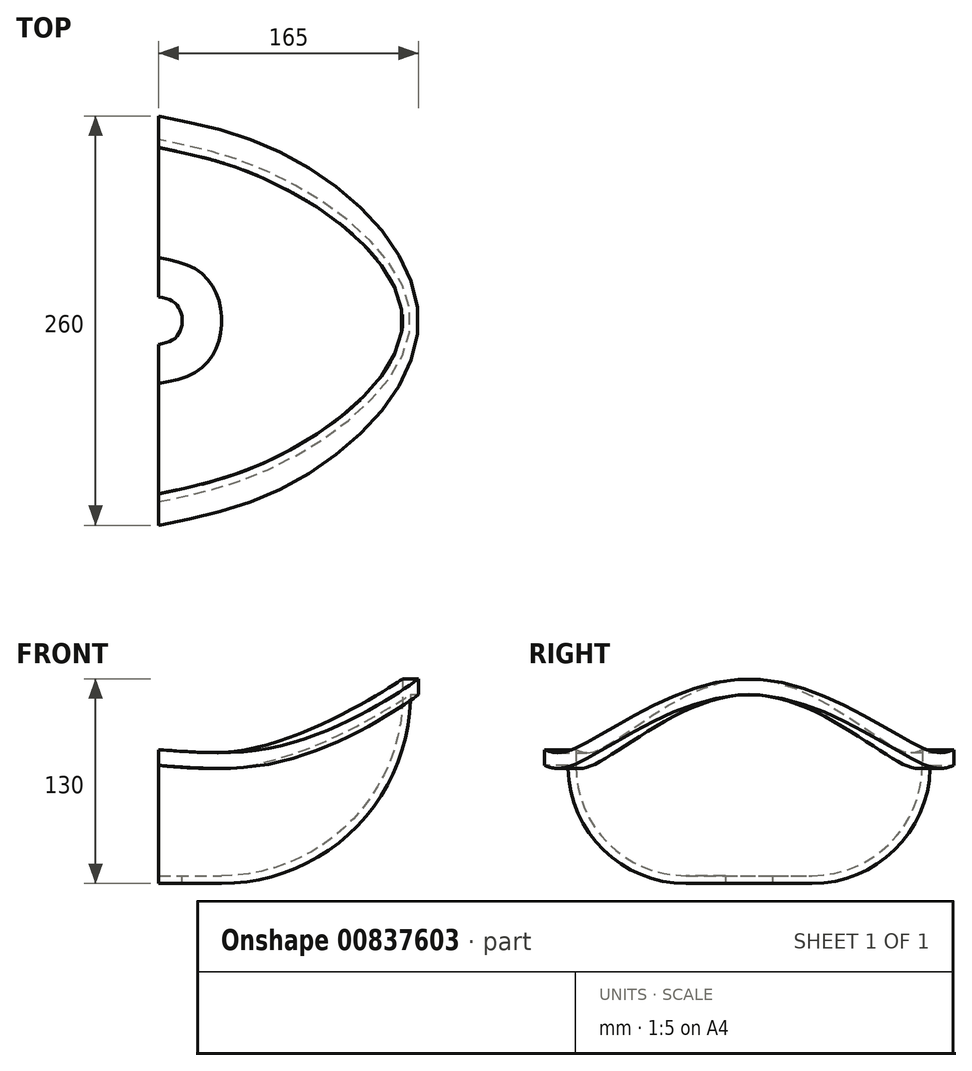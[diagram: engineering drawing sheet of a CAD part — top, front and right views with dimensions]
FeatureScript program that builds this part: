
annotation { "Feature Type Name" : "Feature", "Feature Type Description" : "" }
export const myFeature = defineFeature(function(context is Context, id is Id, definition is map)
    precondition{}
    {
        {
            var Q0;
            Q0=qCreatedBy(makeId("Front.planeOp"),FACE);
            var sketch = newSketch(context, id + "F0", { "sketchPlane" : qUnion([Q0])});
            skLineSegment(sketch, "E0.bottom", {"start": v(15, 5) * mm, "end": v(40, 5) * mm});
            skLineSegment(sketch, "E0.top", {"start": v(15, 0) * mm, "end": v(40, 0) * mm});
            skLineSegment(sketch, "E0.left", {"start": v(15, 5) * mm, "end": v(15, 0) * mm});
            skLineSegment(sketch, "E0.right", {"start": v(40, 5) * mm, "end": v(40, 0) * mm, "construction": true});
            skLineSegment(sketch, "E1.bottom", {"start": v(155, 130) * mm, "end": v(165, 130) * mm});
            skLineSegment(sketch, "E1.top", {"start": v(160, 120) * mm, "end": v(165, 120) * mm});
            skLineSegment(sketch, "E1.left", {"start": v(155, 130) * mm, "end": v(155, 120) * mm});
            skLineSegment(sketch, "E1.right", {"start": v(165, 130) * mm, "end": v(165, 120) * mm});
            skArc(sketch, "E2", {"start": v(40, 0) * mm, "mid": v(124.85, 35.15) * mm, "end": v(160, 120) * mm});
            skArc(sketch, "E3", {"start": v(40, 5) * mm, "mid": v(121.32, 38.68) * mm, "end": v(155, 120) * mm});
            skLineSegment(sketch, "E4", {"start": v(0, 0) * mm, "end": v(0, 50) * mm, "construction": true});
            skSolve(sketch);
        }
        {
            var Q0;
            Q0=sQuery(id+"F0.wireOp",EDGE,"E4");
            cPlane(context, id + "F1", {"entities" : qUnion([Q0]), "cplaneType" : CPlaneType.LINE_ANGLE, "offset" : 25 * mm, "angle" : 30 * degree, "oppositeDirection" : true, "width" : 150 * mm, "height" : 150 * mm});
        }
        {
            var Q0;
            Q0=qCreatedBy(id+"F1.planeOp",FACE);
            var sketch = newSketch(context, id + "F2", { "sketchPlane" : qUnion([Q0])});
            skLineSegment(sketch, "E5.bottom", {"start": v(15, 5) * mm, "end": v(40, 5) * mm});
            skLineSegment(sketch, "E5.top", {"start": v(15, 0) * mm, "end": v(40, 0) * mm});
            skLineSegment(sketch, "E5.left", {"start": v(15, 5) * mm, "end": v(15, 0) * mm});
            skLineSegment(sketch, "E5.right", {"start": v(40, 5) * mm, "end": v(40, 0) * mm, "construction": true});
            skLineSegment(sketch, "E6.bottom", {"start": v(110, 85) * mm, "end": v(130, 85) * mm});
            skLineSegment(sketch, "E6.top", {"start": v(115, 75) * mm, "end": v(130, 75) * mm});
            skLineSegment(sketch, "E6.left", {"start": v(110, 85) * mm, "end": v(110, 75) * mm});
            skLineSegment(sketch, "E6.right", {"start": v(130, 85) * mm, "end": v(130, 75) * mm});
            skArc(sketch, "E7", {"start": v(40, 0) * mm, "mid": v(93.03, 21.97) * mm, "end": v(115, 75) * mm});
            skArc(sketch, "E8", {"start": v(40, 5) * mm, "mid": v(89.5, 25.5) * mm, "end": v(110, 75) * mm});
            skLineSegment(sketch, "E9", {"start": v(0, 0) * mm, "end": v(0, 50) * mm, "construction": true});
            skSolve(sketch);
        }
        {
            var Q0;
            Q0=sQuery(id+"F0.wireOp",EDGE,"E4");
            cPlane(context, id + "F3", {"entities" : qUnion([Q0]), "cplaneType" : CPlaneType.LINE_ANGLE, "offset" : 25 * mm, "angle" : 150 * degree, "oppositeDirection" : true, "width" : 150 * mm, "height" : 150 * mm});
        }
        {
            var Q0;
            Q0=qCreatedBy(id+"F3.planeOp",FACE);
            var sketch = newSketch(context, id + "F4", { "sketchPlane" : qUnion([Q0])});
            skLineSegment(sketch, "E10.bottom", {"start": v(15, 5) * mm, "end": v(40, 5) * mm});
            skLineSegment(sketch, "E10.top", {"start": v(15, 0) * mm, "end": v(40, 0) * mm});
            skLineSegment(sketch, "E10.left", {"start": v(15, 5) * mm, "end": v(15, 0) * mm});
            skLineSegment(sketch, "E10.right", {"start": v(40, 5) * mm, "end": v(40, 0) * mm, "construction": true});
            skLineSegment(sketch, "E11.bottom", {"start": v(110, 85) * mm, "end": v(130, 85) * mm});
            skLineSegment(sketch, "E11.top", {"start": v(115, 75) * mm, "end": v(130, 75) * mm});
            skLineSegment(sketch, "E11.left", {"start": v(110, 85) * mm, "end": v(110, 75) * mm});
            skLineSegment(sketch, "E11.right", {"start": v(130, 85) * mm, "end": v(130, 75) * mm});
            skArc(sketch, "E12", {"start": v(40, 0) * mm, "mid": v(93.03, 21.97) * mm, "end": v(115, 75) * mm});
            skArc(sketch, "E13", {"start": v(40, 5) * mm, "mid": v(89.5, 25.5) * mm, "end": v(110, 75) * mm});
            skLineSegment(sketch, "E14", {"start": v(0, 0) * mm, "end": v(0, 50) * mm, "construction": true});
            skSolve(sketch);
        }
        {
            var Q0;
            Q0=qCreatedBy(makeId("Right.planeOp"),FACE);
            var sketch = newSketch(context, id + "F5", { "sketchPlane" : qUnion([Q0])});
            skLineSegment(sketch, "E15.bottom", {"start": v(15, 5) * mm, "end": v(40, 5) * mm});
            skLineSegment(sketch, "E15.top", {"start": v(15, 0) * mm, "end": v(40, 0) * mm});
            skLineSegment(sketch, "E15.left", {"start": v(15, 5) * mm, "end": v(15, 0) * mm});
            skLineSegment(sketch, "E15.right", {"start": v(40, 5) * mm, "end": v(40, 0) * mm, "construction": true});
            skLineSegment(sketch, "E16.bottom", {"start": v(110, 85) * mm, "end": v(130, 85) * mm});
            skLineSegment(sketch, "E16.top", {"start": v(115, 75) * mm, "end": v(130, 75) * mm});
            skLineSegment(sketch, "E16.left", {"start": v(110, 85) * mm, "end": v(110, 75) * mm});
            skLineSegment(sketch, "E16.right", {"start": v(130, 85) * mm, "end": v(130, 75) * mm});
            skArc(sketch, "E17", {"start": v(40, 0) * mm, "mid": v(93.03, 21.97) * mm, "end": v(115, 75) * mm});
            skArc(sketch, "E18", {"start": v(40, 5) * mm, "mid": v(89.5, 25.5) * mm, "end": v(110, 75) * mm});
            skLineSegment(sketch, "E19", {"start": v(0, 0) * mm, "end": v(0, 50) * mm, "construction": true});
            skSolve(sketch);
        }
        {
            var Q0;
            Q0=sQuery(id+"F5.wireOp",EDGE,"E19");
            cPlane(context, id + "F6", {"entities" : qUnion([Q0]), "cplaneType" : CPlaneType.LINE_ANGLE, "offset" : 25 * mm, "angle" : 180 * degree, "width" : 150 * mm, "height" : 150 * mm});
        }
        {
            var Q0;
            Q0=qCreatedBy(id+"F6.planeOp",FACE);
            var sketch = newSketch(context, id + "F7", { "sketchPlane" : qUnion([Q0])});
            skLineSegment(sketch, "E20.bottom", {"start": v(15, 5) * mm, "end": v(40, 5) * mm});
            skLineSegment(sketch, "E20.top", {"start": v(15, 0) * mm, "end": v(40, 0) * mm});
            skLineSegment(sketch, "E20.left", {"start": v(15, 5) * mm, "end": v(15, 0) * mm});
            skLineSegment(sketch, "E20.right", {"start": v(40, 5) * mm, "end": v(40, 0) * mm, "construction": true});
            skLineSegment(sketch, "E21.bottom", {"start": v(110, 85) * mm, "end": v(130, 85) * mm});
            skLineSegment(sketch, "E21.top", {"start": v(115, 75) * mm, "end": v(130, 75) * mm});
            skLineSegment(sketch, "E21.left", {"start": v(110, 85) * mm, "end": v(110, 75) * mm});
            skLineSegment(sketch, "E21.right", {"start": v(130, 85) * mm, "end": v(130, 75) * mm});
            skArc(sketch, "E22", {"start": v(40, 0) * mm, "mid": v(93.03, 21.97) * mm, "end": v(115, 75) * mm});
            skArc(sketch, "E23", {"start": v(40, 5) * mm, "mid": v(89.5, 25.5) * mm, "end": v(110, 75) * mm});
            skLineSegment(sketch, "E24", {"start": v(0, 0) * mm, "end": v(0, 50) * mm, "construction": true});
            skSolve(sketch);
        }
        {
            var Q0;
            Q0 = qSketchRegion(id + "F7", true);
            var Q1;
            Q1 = qSketchRegion(id + "F4", true);
            var Q2;
            Q2 = qSketchRegion(id + "F0", true);
            var Q3;
            Q3 = qSketchRegion(id + "F2", true);
            var Q4;
            Q4 = qSketchRegion(id + "F5", true);
            loft(context, id + "F8", {"sheetProfilesArray" : [{ "sheetProfileEntities" : qUnion([Q0]) }, { "sheetProfileEntities" : qUnion([Q1]) }, { "sheetProfileEntities" : qUnion([Q2]) }, { "sheetProfileEntities" : qUnion([Q3]) }, { "sheetProfileEntities" : qUnion([Q4]) }]});
        }
    });
